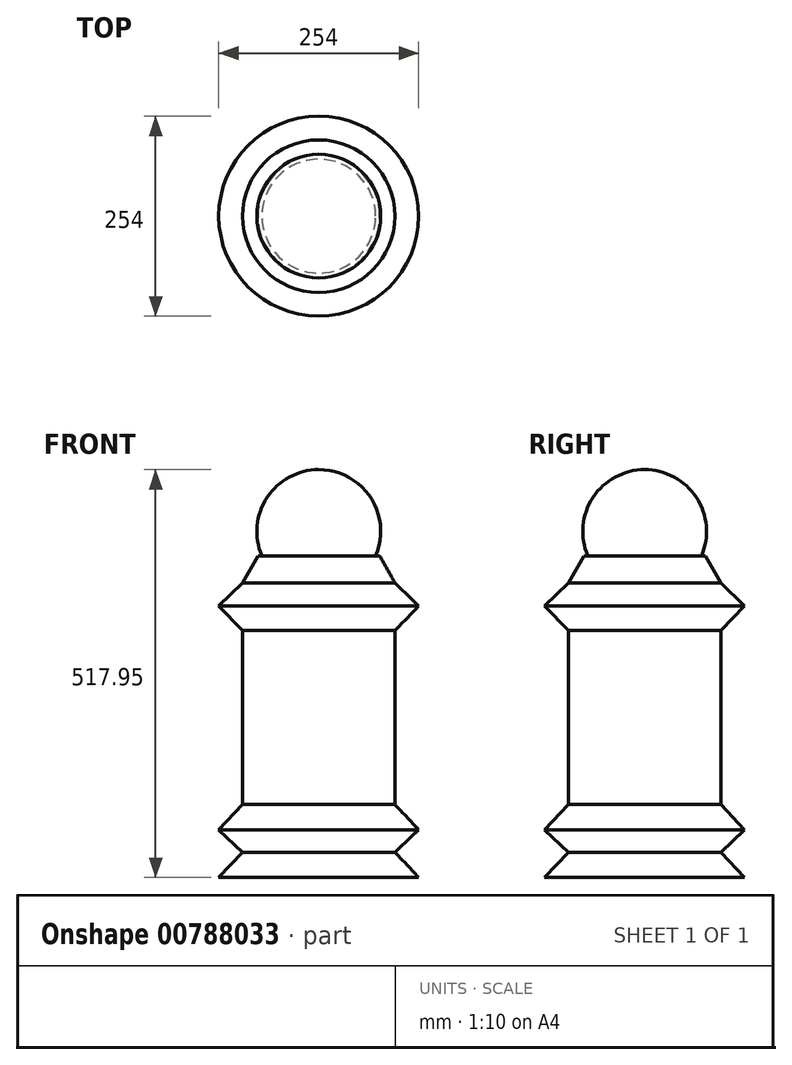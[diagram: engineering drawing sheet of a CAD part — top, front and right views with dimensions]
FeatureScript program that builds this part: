
annotation { "Feature Type Name" : "Feature", "Feature Type Description" : "" }
export const myFeature = defineFeature(function(context is Context, id is Id, definition is map)
    precondition{}
    {
        {
            var Q0;
            Q0=qCreatedBy(makeId("Front.planeOp"),FACE);
            var sketch = newSketch(context, id + "F0", { "sketchPlane" : qUnion([Q0])});
            skLineSegment(sketch, "E0", {"start": v(0, -313.5) * mm, "end": v(-127, -313.5) * mm});
            skLineSegment(sketch, "E1", {"start": v(-127, -313.5) * mm, "end": v(-96.8, -281.53) * mm});
            skLineSegment(sketch, "E2", {"start": v(-96.8, -281.53) * mm, "end": v(-127, -253.01) * mm});
            skLineSegment(sketch, "E3", {"start": v(-127, -253.01) * mm, "end": v(-96.8, -221.04) * mm});
            skLineSegment(sketch, "E4", {"start": v(-96.8, -221.04) * mm, "end": v(-96.8, 0) * mm});
            skLineSegment(sketch, "E5", {"start": v(-96.8, 0) * mm, "end": v(-127, 31.08) * mm});
            skLineSegment(sketch, "E6", {"start": v(-127, 31.08) * mm, "end": v(-96.8, 60.42) * mm});
            skLineSegment(sketch, "E7", {"start": v(-96.8, 60.42) * mm, "end": v(-77.27, 95.03) * mm});
            skLineSegment(sketch, "E8", {"start": v(0, 684.73) * mm, "end": v(0, -549.74) * mm});
            skLineSegment(sketch, "E9", {"start": v(-77.27, 95.03) * mm, "end": v(-72.3, 95.03) * mm});
            skLineSegment(sketch, "E10", {"start": v(-127, -313.5) * mm, "end": v(-127, -253.01) * mm});
            skCircle(sketch, "E11", {"center": v(0, 125.84) * mm, "radius": 78.6 * mm});
            skSolve(sketch);
        }
        {
            var Q0;
            {var subQ2=sQuery(id+"F0.wireOp",EDGE,"E0");Q0=makeQuery(id+"F0.imprint","IMPRINT",FACE,{"disambiguationData":[TD([[makeQuery(id+"F0.imprint","IMPRINT",EDGE,{"derivedFrom":subQ2}),-1.0]])]});}
            var Q1;
            {var subQ0=sQuery(id+"F0.wireOp",EDGE,"E11");var subQ1=sQuery(id+"F0.wireOp",EDGE,"E8");var subQ2=makeQuery(id+"F0.imprint","INTERSECT",VERTEX,{"disambiguationData":[OD(0.0)],"derivedFrom":[subQ1,subQ0]});Q1=makeQuery(id+"F0.imprint","IMPRINT",FACE,{"disambiguationData":[TD([[makeQuery(id+"F0.imprint","IMPRINT",EDGE,{"disambiguationData":[TD([[subQ2,-1.0]])],"derivedFrom":subQ1}),-1.0]])]});}
            var Q2;
            Q2=sQuery(id+"F0.wireOp",EDGE,"E8");
            revolve(context, id + "F1", {"surfaceOperationType" : NewSurfaceOperationType.NEW, "entities" : qUnion([Q0, Q1]), "axis" : qUnion([Q2]), "revolveType" : RevolveType.FULL});
        }
    });
